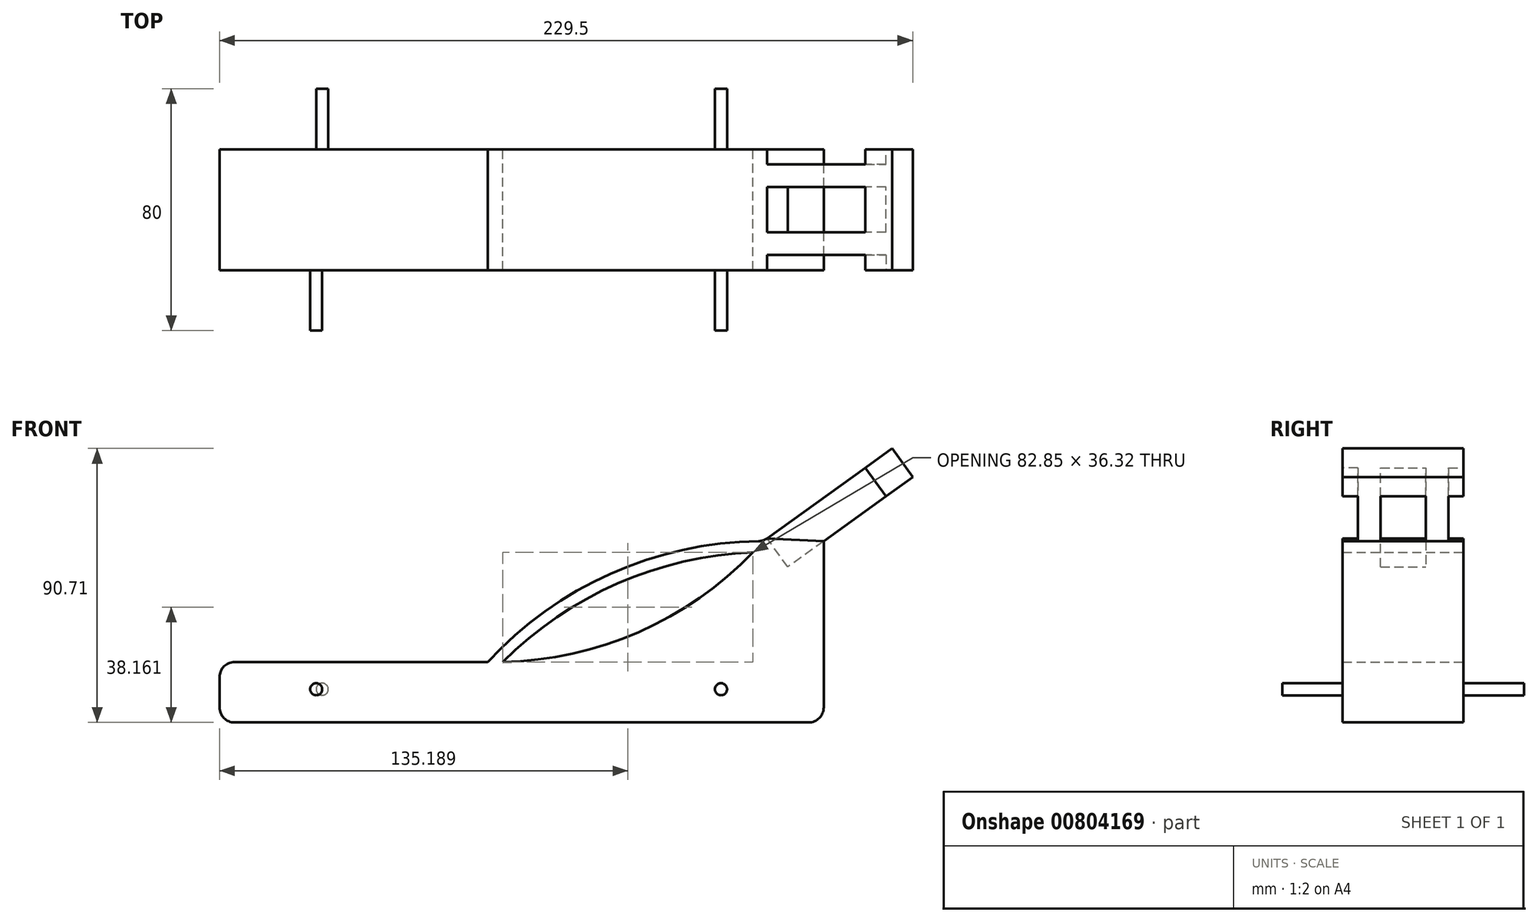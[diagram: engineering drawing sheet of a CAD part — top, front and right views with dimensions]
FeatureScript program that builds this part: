
annotation { "Feature Type Name" : "Feature", "Feature Type Description" : "" }
export const myFeature = defineFeature(function(context is Context, id is Id, definition is map)
    precondition{}
    {
        {
            var Q0;
            Q0=qCreatedBy(makeId("Front.planeOp"),FACE);
            var sketch = newSketch(context, id + "F0", { "sketchPlane" : qUnion([Q0])});
            skLineSegment(sketch, "E0", {"start": v(0, 0) * mm, "end": v(0, 20) * mm});
            skLineSegment(sketch, "E1", {"start": v(0, 0) * mm, "end": v(200, 0) * mm});
            skLineSegment(sketch, "E2", {"start": v(200, 0) * mm, "end": v(200, 60) * mm});
            skLineSegment(sketch, "E3", {"start": v(88.77, 20) * mm, "end": v(0, 20) * mm});
            skLineSegment(sketch, "E4", {"start": v(200, 60) * mm, "end": v(180, 60) * mm});
            skArc(sketch, "E5", {"start": v(88.77, 20) * mm, "mid": v(138.8, 29.94) * mm, "end": v(180, 60) * mm});
            skLineSegment(sketch, "E6", {"start": v(180, 60) * mm, "end": v(222.67, 90.71) * mm});
            skLineSegment(sketch, "E7", {"start": v(222.67, 90.71) * mm, "end": v(229.5, 81.23) * mm});
            skLineSegment(sketch, "E8", {"start": v(229.5, 81.23) * mm, "end": v(200, 60) * mm});
            skArc(sketch, "E9", {"start": v(180, 60) * mm, "mid": v(130.2, 49.56) * mm, "end": v(88.77, 20) * mm});
            skArc(sketch, "E10", {"start": v(176.61, 56.32) * mm, "mid": v(131.76, 45.98) * mm, "end": v(93.77, 20) * mm});
            skSolve(sketch);
        }
        {
            var Q0;
            Q0 = qSketchRegion(id + "F0", true);
            extrude(context, id + "F1", {"entities" : qUnion([Q0]), "depth" : 40 * mm, "offsetDistance" : 25 * mm});
        }
        {
            var Q0;
            Q0=makeQuery(id+"F1.opExtrude","SWEPT_EDGE",EDGE,{"disambiguationData":[OSD([sQuery(id+"F0.wireOp",EDGE,"E0"),sQuery(id+"F0.wireOp",EDGE,"VwHznC4o-IUDD-ZUbm-hCj7-YLazc3NbNDuq")])]});
            var Q1;
            Q1=makeQuery(id+"F1.opExtrude","SWEPT_EDGE",EDGE,{"disambiguationData":[OSD([sQuery(id+"F0.wireOp",EDGE,"E2"),sQuery(id+"F0.wireOp",EDGE,"VMn3sJ2O-N24a-Yy71-zCfI-SlEi6difZZmf")])]});
            fillet(context, id + "F2", {"entities" : qUnion([Q0, Q1]), "radius" : 5 * mm, "tangentPropagation" : true, "allowEdgeOverflow" : false});
        }
        {
            var Q0;
            Q0=makeQuery(id+"F1.opExtrude","CAP_FACE",FACE,{"disambiguationData":[OSD([sQuery(id+"F0.wireOp",EDGE,"E0"),sQuery(id+"F0.wireOp",EDGE,"E1"),sQuery(id+"F0.wireOp",EDGE,"E2"),sQuery(id+"F0.wireOp",EDGE,"VMn3sJ2O-N24a-Yy71-zCfI-SlEi6difZZmf"),sQuery(id+"F0.wireOp",EDGE,"VwHznC4o-IUDD-ZUbm-hCj7-YLazc3NbNDuq")])],"isStart":false});
            var sketch = newSketch(context, id + "F3", { "sketchPlane" : qUnion([Q0])});
            skCircle(sketch, "E11", {"center": v(32, 11) * mm, "radius": 2 * mm});
            skCircle(sketch, "E12", {"center": v(166, 11) * mm, "radius": 2 * mm});
            skSolve(sketch);
        }
        {
            var Q0;
            Q0=makeQuery(id+"F1.opExtrude","CAP_FACE",FACE,{"disambiguationData":[OSD([sQuery(id+"F0.wireOp",EDGE,"E0"),sQuery(id+"F0.wireOp",EDGE,"E1"),sQuery(id+"F0.wireOp",EDGE,"E2"),sQuery(id+"F0.wireOp",EDGE,"VMn3sJ2O-N24a-Yy71-zCfI-SlEi6difZZmf"),sQuery(id+"F0.wireOp",EDGE,"VwHznC4o-IUDD-ZUbm-hCj7-YLazc3NbNDuq")])],"isStart":true});
            var sketch = newSketch(context, id + "F4", { "sketchPlane" : qUnion([Q0])});
            skCircle(sketch, "E13", {"center": v(-166, 11) * mm, "radius": 2 * mm});
            skCircle(sketch, "E14", {"center": v(-34, 11) * mm, "radius": 2 * mm});
            skSolve(sketch);
        }
        {
            var Q0;
            Q0=makeQuery(id+"F1.opExtrude","SWEPT_EDGE",EDGE,{"disambiguationData":[OSD([sQuery(id+"F0.wireOp",EDGE,"E4"),sQuery(id+"F0.wireOp",EDGE,"E5")])]});
            fillet(context, id + "F5", {"entities" : qUnion([Q0]), "radius" : 5 * mm, "tangentPropagation" : true, "allowEdgeOverflow" : false});
        }
        {
            var Q0;
            Q0=makeQuery(id+"F1.opExtrude","CAP_FACE",FACE,{"disambiguationData":[OSD([sQuery(id+"F0.wireOp",EDGE,"E0"),sQuery(id+"F0.wireOp",EDGE,"E1"),sQuery(id+"F0.wireOp",EDGE,"E2"),sQuery(id+"F0.wireOp",EDGE,"E3"),sQuery(id+"F0.wireOp",EDGE,"E5"),sQuery(id+"F0.wireOp",EDGE,"E6"),sQuery(id+"F0.wireOp",EDGE,"E7"),sQuery(id+"F0.wireOp",EDGE,"E8")])],"isStart":false});
            var sketch = newSketch(context, id + "F6", { "sketchPlane" : qUnion([Q0])});
            skLineSegment(sketch, "E15", {"start": v(200, 60) * mm, "end": v(181.3, 60.93) * mm});
            skLineSegment(sketch, "E16", {"start": v(181.3, 60.93) * mm, "end": v(213.76, 84.3) * mm});
            skLineSegment(sketch, "E17", {"start": v(213.76, 84.3) * mm, "end": v(220.58, 74.82) * mm});
            skLineSegment(sketch, "E18", {"start": v(220.58, 74.82) * mm, "end": v(200, 60) * mm});
            skSolve(sketch);
        }
        {
            var Q0;
            Q0 = qSketchRegion(id + "F6", true);
            extrude(context, id + "F7", {"entities" : qUnion([Q0]), "operationType" : NewBodyOperationType.REMOVE, "oppositeDirection" : true, "depth" : 5 * mm, "offsetDistance" : 25 * mm});
        }
        {
            var Q0;
            Q0=makeQuery(id+"F1.opExtrude","CAP_FACE",FACE,{"disambiguationData":[OSD([sQuery(id+"F0.wireOp",EDGE,"E0"),sQuery(id+"F0.wireOp",EDGE,"E1"),sQuery(id+"F0.wireOp",EDGE,"E2"),sQuery(id+"F0.wireOp",EDGE,"E3"),sQuery(id+"F0.wireOp",EDGE,"E5"),sQuery(id+"F0.wireOp",EDGE,"E6"),sQuery(id+"F0.wireOp",EDGE,"E7"),sQuery(id+"F0.wireOp",EDGE,"E8")])],"isStart":true});
            var sketch = newSketch(context, id + "F8", { "sketchPlane" : qUnion([Q0])});
            skLineSegment(sketch, "E19", {"start": v(-200, 60) * mm, "end": v(-181.3, 60.93) * mm});
            skLineSegment(sketch, "E20", {"start": v(-181.3, 60.93) * mm, "end": v(-213.76, 84.3) * mm});
            skLineSegment(sketch, "E21", {"start": v(-213.76, 84.3) * mm, "end": v(-220.58, 74.82) * mm});
            skLineSegment(sketch, "E22", {"start": v(-220.58, 74.82) * mm, "end": v(-200, 60) * mm});
            skSolve(sketch);
        }
        {
            var Q0;
            Q0 = qSketchRegion(id + "F8", true);
            extrude(context, id + "F9", {"entities" : qUnion([Q0]), "operationType" : NewBodyOperationType.REMOVE, "oppositeDirection" : true, "depth" : 5 * mm, "offsetDistance" : 25 * mm});
        }
        {
            var Q0;
            Q0=makeQuery(id+"F1.opExtrude","SWEPT_FACE",FACE,{"disambiguationData":[OSD([sQuery(id+"F0.wireOp",EDGE,"E6")])]});
            var sketch = newSketch(context, id + "F10", { "sketchPlane" : qUnion([Q0])});
            skLineSegment(sketch, "E23", {"start": v(222.74, -12.5) * mm, "end": v(182.74, -12.5) * mm});
            skLineSegment(sketch, "E24", {"start": v(182.74, -12.5) * mm, "end": v(182.74, -27.5) * mm});
            skLineSegment(sketch, "E25", {"start": v(182.74, -27.5) * mm, "end": v(222.74, -27.5) * mm});
            skLineSegment(sketch, "E26", {"start": v(222.74, -27.5) * mm, "end": v(222.74, -12.5) * mm});
            skSolve(sketch);
        }
        {
            var Q0;
            Q0 = qSketchRegion(id + "F10", true);
            extrude(context, id + "F11", {"entities" : qUnion([Q0]), "operationType" : NewBodyOperationType.REMOVE, "oppositeDirection" : true, "depth" : 11.68 * mm, "offsetDistance" : 25 * mm});
        }
        {
            var Q0;
            Q0 = qSketchRegion(id + "F3", true);
            extrude(context, id + "F12", {"entities" : qUnion([Q0]), "operationType" : NewBodyOperationType.ADD, "depth" : 20 * mm, "offsetDistance" : 25 * mm});
        }
        {
            var Q0;
            Q0 = qSketchRegion(id + "F4", true);
            extrude(context, id + "F13", {"entities" : qUnion([Q0]), "operationType" : NewBodyOperationType.ADD, "depth" : 20 * mm, "offsetDistance" : 25 * mm});
        }
    });
